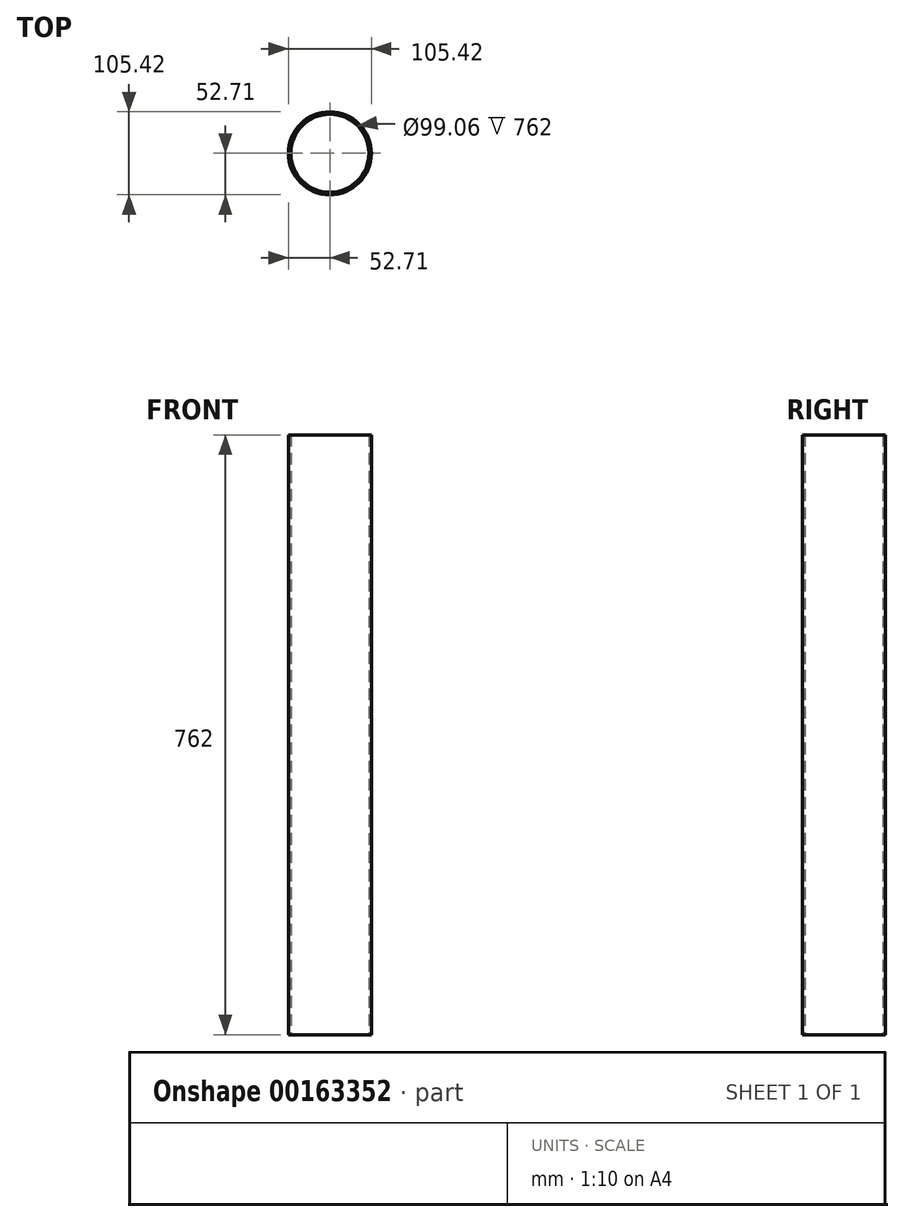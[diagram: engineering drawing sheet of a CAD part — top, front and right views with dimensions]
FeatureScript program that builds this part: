
annotation { "Feature Type Name" : "Feature", "Feature Type Description" : "" }
export const myFeature = defineFeature(function(context is Context, id is Id, definition is map)
    precondition{}
    {
        {
            var Q0;
            Q0=qCreatedBy(makeId("Top.planeOp"),FACE);
            var sketch = newSketch(context, id + "F0", { "sketchPlane" : qUnion([Q0])});
            skCircle(sketch, "E0", {"center": v(0, 0) * mm, "radius": 49.53 * mm});
            skCircle(sketch, "E1", {"center": v(0, 0) * mm, "radius": 52.7 * mm});
            skSolve(sketch);
        }
        {
            var Q0;
            Q0=makeQuery(id+"F0.imprint","IMPRINT",FACE,{"disambiguationData":[TD([[makeQuery(id+"F0.imprint","IMPRINT",EDGE,{"derivedFrom":sQuery(id+"F0.wireOp",EDGE,"E0")}),-1.0]])]});
            extrude(context, id + "F1", {"entities" : qUnion([Q0]), "depth" : 762 * mm});
        }
        {
            var Q0;
            Q0=qCreatedBy(makeId("Front.planeOp"),FACE);
            var sketch = newSketch(context, id + "F2", { "sketchPlane" : qUnion([Q0])});
            skLineSegment(sketch, "E2", {"start": v(0, 0) * mm, "end": v(52.7, 0) * mm});
            skLineSegment(sketch, "E3", {"start": v(0, 0) * mm, "end": v(-52.7, 0) * mm});
            skLineSegment(sketch, "E4", {"start": v(-52.7, 0) * mm, "end": v(-52.7, 190.5) * mm});
            skLineSegment(sketch, "E5", {"start": v(-52.7, 190.5) * mm, "end": v(52.7, 190.5) * mm});
            skLineSegment(sketch, "E6", {"start": v(52.7, 190.5) * mm, "end": v(52.7, 0) * mm});
            skSolve(sketch);
        }
    });
